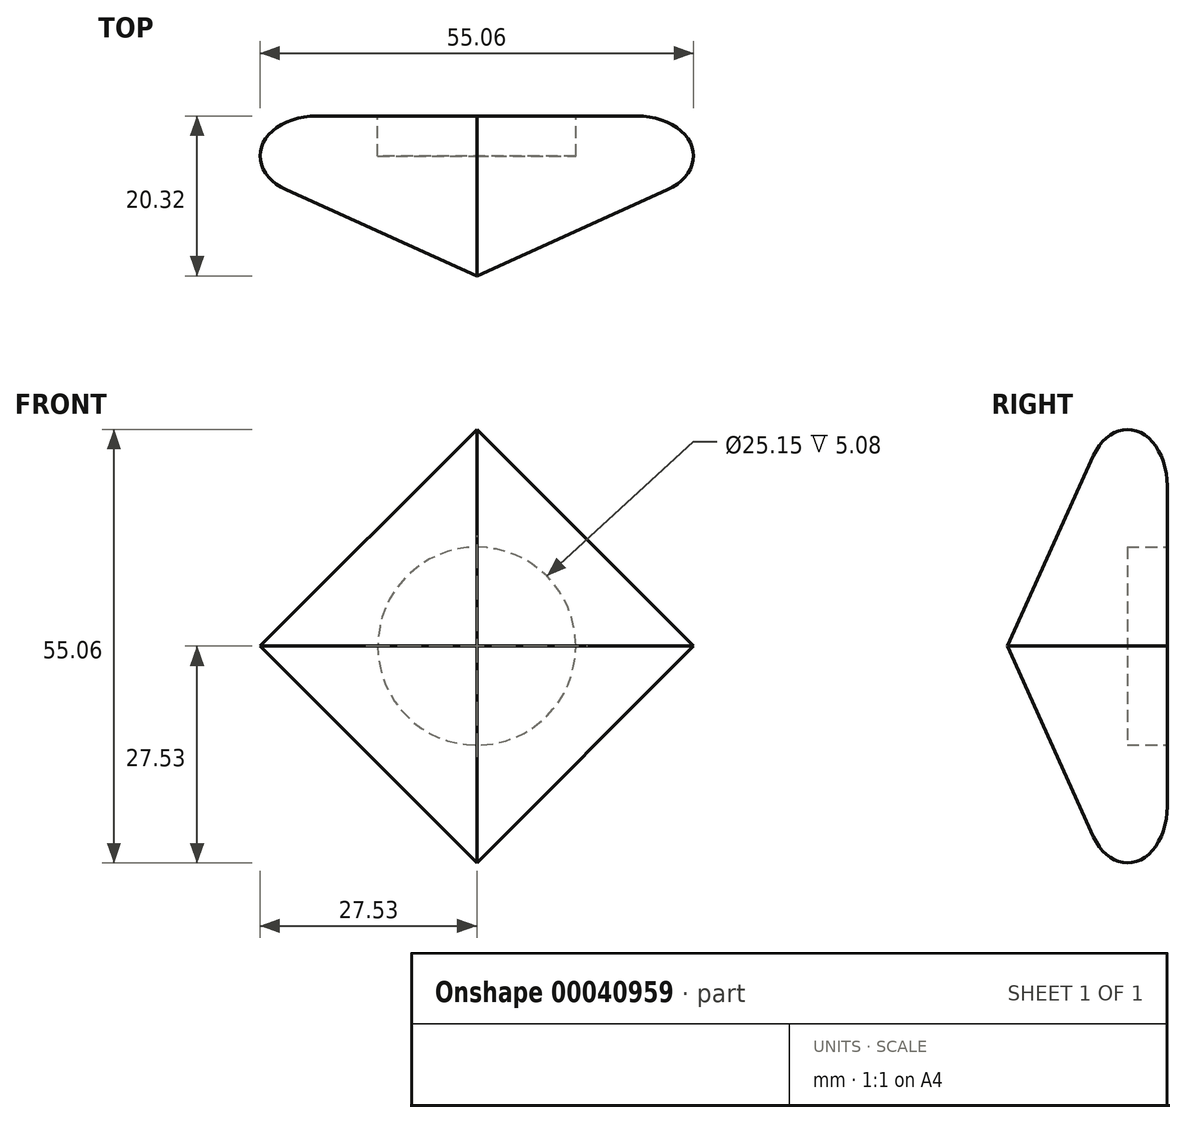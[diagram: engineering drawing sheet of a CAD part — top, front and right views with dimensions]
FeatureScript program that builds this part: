
annotation { "Feature Type Name" : "Feature", "Feature Type Description" : "" }
export const myFeature = defineFeature(function(context is Context, id is Id, definition is map)
    precondition{}
    {
        {
            var Q0;
            Q0=qCreatedBy(makeId("Front.planeOp"),FACE);
            var sketch = newSketch(context, id + "F0", { "sketchPlane" : qUnion([Q0])});
            skCircle(sketch, "E0.cCircle", {"center": v(0, 0) * mm, "radius": 31.75 * mm, "construction": true});
            skLineSegment(sketch, "E0.0", {"start": v(0, -44.9) * mm, "end": v(-44.9, 0) * mm});
            skLineSegment(sketch, "E0.1", {"start": v(-44.9, 0) * mm, "end": v(0, 44.9) * mm});
            skLineSegment(sketch, "E0.2", {"start": v(0, 44.9) * mm, "end": v(44.9, 0) * mm});
            skLineSegment(sketch, "E0.3", {"start": v(44.9, 0) * mm, "end": v(0, -44.9) * mm});
            skPoint(sketch, "E0.0.midPoint", {"position": v(-22.45, -22.45) * mm});
            skSolve(sketch);
        }
        {
            var Q0;
            Q0=qCreatedBy(makeId("Top.planeOp"),FACE);
            var sketch = newSketch(context, id + "F1", { "sketchPlane" : qUnion([Q0])});
            skPoint(sketch, "E1", {"position": v(0, -20.32) * mm});
            skSolve(sketch);
        }
        {
            var Q0;
            Q0=makeQuery(id+"F0.imprint","IMPRINT",FACE,{"disambiguationData":[TD([[makeQuery(id+"F0.imprint","IMPRINT",EDGE,{"derivedFrom":sQuery(id+"F0.wireOp",EDGE,"E0.0")}),-1.0]])]});
            var Q1;
            Q1=sQuery(id+"F1.wireOp",VERTEX,"E1");
            loft(context, id + "F2", {"sheetProfilesArray" : [{ "sheetProfileEntities" : qUnion([Q0]) }, { "sheetProfileEntities" : qUnion([Q1]) }]});
        }
        {
            var Q0;
            Q0=makeQuery(id+"F2.opLoft","CAP_FACE",FACE,{"disambiguationData":[OSD([makeQuery(id+"F0.imprint","IMPRINT",FACE,{"disambiguationData":[TD([[makeQuery(id+"F0.imprint","IMPRINT",EDGE,{"derivedFrom":sQuery(id+"F0.wireOp",EDGE,"E0.0")}),-1.0]])]})])],"isStart":true});
            fillet(context, id + "F3", {"entities" : qUnion([Q0]), "radius" : 5.08 * mm, "tangentPropagation" : true, "allowEdgeOverflow" : false});
        }
        {
            var Q0;
            Q0=makeQuery(id+"F2.opLoft","CAP_FACE",FACE,{"disambiguationData":[OSD([makeQuery(id+"F0.imprint","IMPRINT",FACE,{"disambiguationData":[TD([[makeQuery(id+"F0.imprint","IMPRINT",EDGE,{"derivedFrom":sQuery(id+"F0.wireOp",EDGE,"E0.0")}),-1.0]])]})])],"isStart":true});
            var sketch = newSketch(context, id + "F4", { "sketchPlane" : qUnion([Q0])});
            skCircle(sketch, "E2", {"center": v(0, 0) * mm, "radius": 12.57 * mm});
            skSolve(sketch);
        }
        {
            var Q0;
            Q0=qSketchRegion(id+"F4",true);
            extrude(context, id + "F5", {"entities" : qUnion([Q0]), "operationType" : NewBodyOperationType.REMOVE, "oppositeDirection" : true, "depth" : 5.08 * mm});
        }
    });
